# Revit family: Kitchen_Taps-Mixers_hansgrohe_74800JPN-Zesis-M33-Single-lever-kitchen_2111
name_source: partatom
category: Plumbing Fixtures
revit_build: Autodesk Revit 2018 (Build: 20170223_1515(x64)
units: mm (PartAtom-declared; Revit-internal decimal feet)

## family parameters
Always vertical = No
Cut with Voids When Loaded = No
OmniClass Number = 23.45.55.17
OmniClass Title = Mixing Faucets
Part Type = Normal
Room Calculation Point = No
Round Connector Dimension = Use Diameter
Shared = No
Work Plane-Based = Yes

## types (2) — shared parameters
Always visible = Yes
BIMobject category = Taps & Mixers
Cold Water Inlet = 10 mm
Cold Water Inlet Description = Cold Water Inlet 9.5 mm
Default Elevation = 1219.2 mm  [stored 4 ft]
Description = Zesis M33 Single lever kitchen mixer 150, pull-out spray, 2jet
Design country = Germany
Edition number = 1
Hot Water Inlet = 10 mm
Hot Water Inlet Description = Hot Water Inlet 9.5 mm
IFC Classification = Valve
Manufacturer = Hansgrohe
Manufacturer country = Germany
Manufacturer name = hansgrohe
Masterformat 2014 Code = 22 41 39
Masterformat 2014 Description = Residential Faucets, Supplies, and Trim
Model = 74800JPN
OmniClass Code = 23-31 11 15 11
OmniClass Description = Sink Cartridge Faucets
Product Guid = d69c6739-ae97-4fc9-a003-bab1a0309ca7
Product SKU = 74800JPN
Product data url = https://www.bimobject.com
Product family = Zesis M33
Product group = Kitchen mixers
Product name = 74800JPN Zesis M33 Single lever kitchen mixer 150, pull-out spray, 2jet
QR code = https://www.bimobject.com
URL = https://www.hansgrohe.com
Uniclass 2015 Code = Pr_40_20_87_84
Uniclass 2015 Name = Sink taps
Uniformat II Code = D2010
Uniformat II Description = Plumbing Fixtures
Weight Net (Kg) = 1.9

## per-type parameters (varying)
| type | Material 1 |
| 674 Matte Black | Hansgrohe - Metal - 674 Matte Black |
| 004 Chrome | Hansgrohe - Metal - 004 Chrome |

note: [stored X ft] marks values corroborated as IEEE doubles in the binary element streams (Revit-internal decimal feet)

## geometry (parser evidence)
native form markers: Sweep x2
no freeform markers — native parametric forms only
